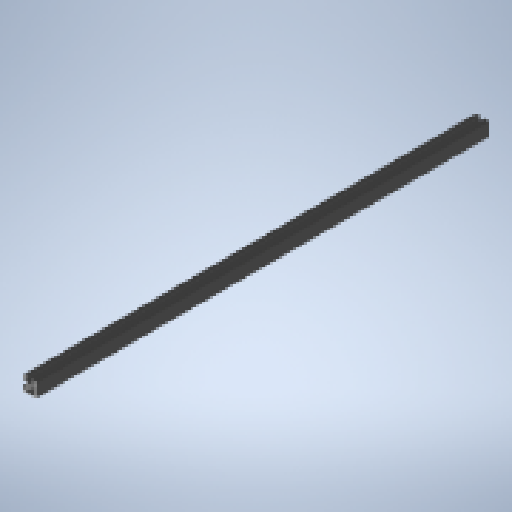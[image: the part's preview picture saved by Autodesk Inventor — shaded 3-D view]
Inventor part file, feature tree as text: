
AUTODESK INVENTOR PART (.ipt)
format: ipt  version: 2024 (Build 280153000, 153)  size: 257,536 bytes
history: native  units: mm
features: other x7, thread x2, sketch x2, extrude x1, hole x1
ambient origin geometry x8: Origin, YZ Plane, XZ Plane, XY Plane, X Axis, Y Axis, Z Axis, Center Point
bodies: Solid1 (feature_tree)
feature tree (13):
  extrude  "Extrusion1"  TaperAngle=0.0deg  [1 undecoded]
  hole  "Hole1"  [1 undecoded]
  other  "C1_XY"
  other  "C1_YZ"
  other  "C1_ZX"
  other  "C1_X"
  other  "C1_Y"
  other  "C1_Z"
  other  "C1_Center"
  thread  "Thread1"  [1 undecoded]
  thread  "Thread2"  [1 undecoded]
  sketch  "Sketch_64"  dims[d2=4.2mm d3=6.0mm d4=4.0mm d5=2.0mm d6=90.0deg d7=680.0mm d8=0.0mm d9=0.0mm d10=10.0mm d11=0.0mm d12=10.0mm d13=0.0mm]
  sketch  "Sketch2"  dims[d0=650.0mm d1=0.0mm]
note: 4 required parameter values undecoded (feature->parameter linkage not recoverable at this tier; creation-order binding heuristic only, values carry confidence <= 0.55)
